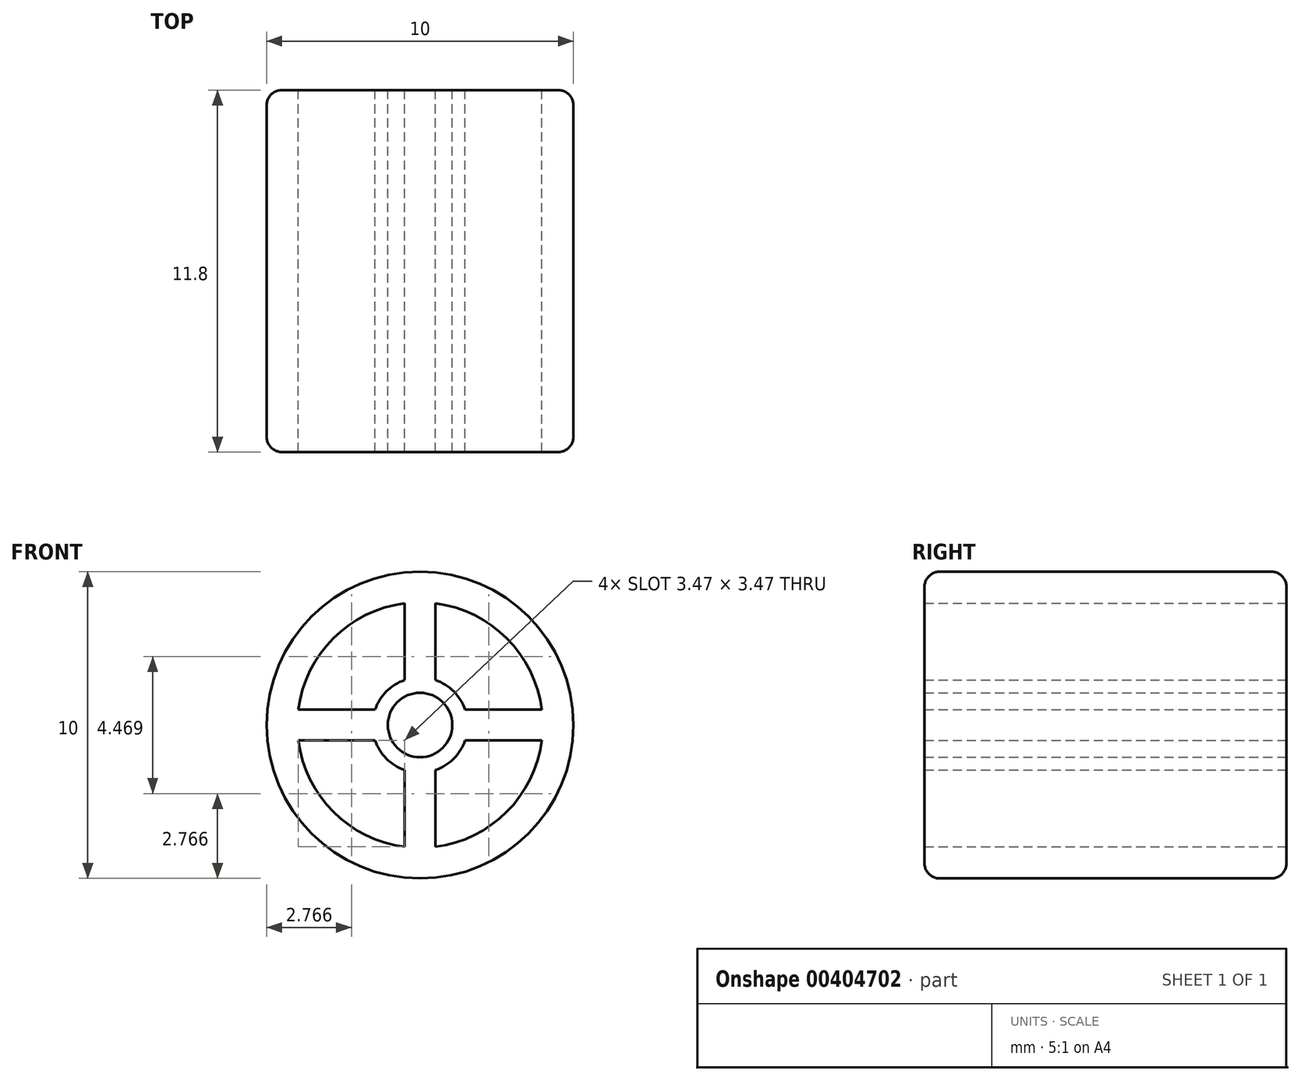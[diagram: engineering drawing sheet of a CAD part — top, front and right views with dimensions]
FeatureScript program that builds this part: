
annotation { "Feature Type Name" : "Feature", "Feature Type Description" : "" }
export const myFeature = defineFeature(function(context is Context, id is Id, definition is map)
    precondition{}
    {
        {
            var Q0;
            Q0=qCreatedBy(makeId("Front.planeOp"),FACE);
            var sketch = newSketch(context, id + "F0", { "sketchPlane" : qUnion([Q0])});
            skArc(sketch, "E0", {"start": v(-1.47, -0.5) * mm, "mid": v(-1.1, -1.1) * mm, "end": v(-0.5, -1.47) * mm});
            skCircle(sketch, "E1", {"center": v(0, 0) * mm, "radius": 1.05 * mm});
            skArc(sketch, "E2", {"start": v(-0.5, 3.97) * mm, "mid": v(-2.83, 2.83) * mm, "end": v(-3.97, 0.5) * mm});
            skCircle(sketch, "E3", {"center": v(0, 0) * mm, "radius": 5 * mm});
            skLineSegment(sketch, "E4.bottom", {"start": v(3.97, -0.5) * mm, "end": v(1.47, -0.5) * mm});
            skLineSegment(sketch, "E4.top", {"start": v(3.97, 0.5) * mm, "end": v(1.47, 0.5) * mm});
            skLineSegment(sketch, "E5.left", {"start": v(0.5, 3.97) * mm, "end": v(0.5, 1.47) * mm});
            skLineSegment(sketch, "E5.right", {"start": v(-0.5, 3.97) * mm, "end": v(-0.5, 1.47) * mm});
            skPoint(sketch, "E6.orphan", {"position": v(-0.5, 4.97) * mm});
            skPoint(sketch, "E7.orphan", {"position": v(0.5, 4.97) * mm});
            skArc(sketch, "E8.trimOffspring", {"start": v(-3.97, -0.5) * mm, "mid": v(-2.83, -2.83) * mm, "end": v(-0.5, -3.97) * mm});
            skPoint(sketch, "E4.right.end.orphan", {"position": v(-4.97, 0.5) * mm});
            skPoint(sketch, "E4.right.start.orphan", {"position": v(-4.97, -0.5) * mm});
            skLineSegment(sketch, "E9.trimOffspring", {"start": v(-1.47, 0.5) * mm, "end": v(-3.97, 0.5) * mm});
            skLineSegment(sketch, "E10.trimOffspring", {"start": v(-1.47, -0.5) * mm, "end": v(-3.97, -0.5) * mm});
            skLineSegment(sketch, "E11.trimOffspring", {"start": v(-0.5, -1.47) * mm, "end": v(-0.5, -3.97) * mm});
            skLineSegment(sketch, "E12.trimOffspring", {"start": v(0.5, -1.47) * mm, "end": v(0.5, -3.97) * mm});
            skArc(sketch, "E13.trimOffspring", {"start": v(-0.5, 1.47) * mm, "mid": v(-1.1, 1.1) * mm, "end": v(-1.47, 0.5) * mm});
            skArc(sketch, "E14.trimOffspring", {"start": v(1.47, 0.5) * mm, "mid": v(1.1, 1.1) * mm, "end": v(0.5, 1.47) * mm});
            skArc(sketch, "E15.trimOffspring", {"start": v(0.5, -1.47) * mm, "mid": v(1.1, -1.1) * mm, "end": v(1.47, -0.5) * mm});
            skArc(sketch, "E16.trimOffspring", {"start": v(0.5, -3.97) * mm, "mid": v(2.83, -2.83) * mm, "end": v(3.97, -0.5) * mm});
            skPoint(sketch, "E5.top.end.orphan", {"position": v(-0.5, -4.97) * mm});
            skPoint(sketch, "E5.top.start.orphan", {"position": v(0.5, -4.97) * mm});
            skPoint(sketch, "E17.orphan", {"position": v(4.97, 0.5) * mm});
            skArc(sketch, "E18.trimOffspring", {"start": v(3.97, 0.5) * mm, "mid": v(2.83, 2.83) * mm, "end": v(0.5, 3.97) * mm});
            skPoint(sketch, "E19.orphan", {"position": v(4.97, -0.5) * mm});
            skSolve(sketch);
        }
        {
            var Q0;
            Q0 = qSketchRegion(id + "F0", true);
            extrude(context, id + "F1", {"entities" : qUnion([Q0]), "depth" : 11.8 * mm, "symmetric" : true});
        }
        {
            var Q0;
            Q0=makeQuery(id+"F1.opExtrude","CAP_EDGE",EDGE,{"disambiguationData":[OSD([sQuery(id+"F0.wireOp",EDGE,"E3")])],"isStart":false});
            var Q1;
            Q1=makeQuery(id+"F1.opExtrude","CAP_EDGE",EDGE,{"disambiguationData":[OSD([sQuery(id+"F0.wireOp",EDGE,"E3")])],"isStart":true});
            fillet(context, id + "F2", {"entities" : qUnion([Q0, Q1]), "radius" : .5 * mm, "tangentPropagation" : true, "allowEdgeOverflow" : false});
        }
    });
